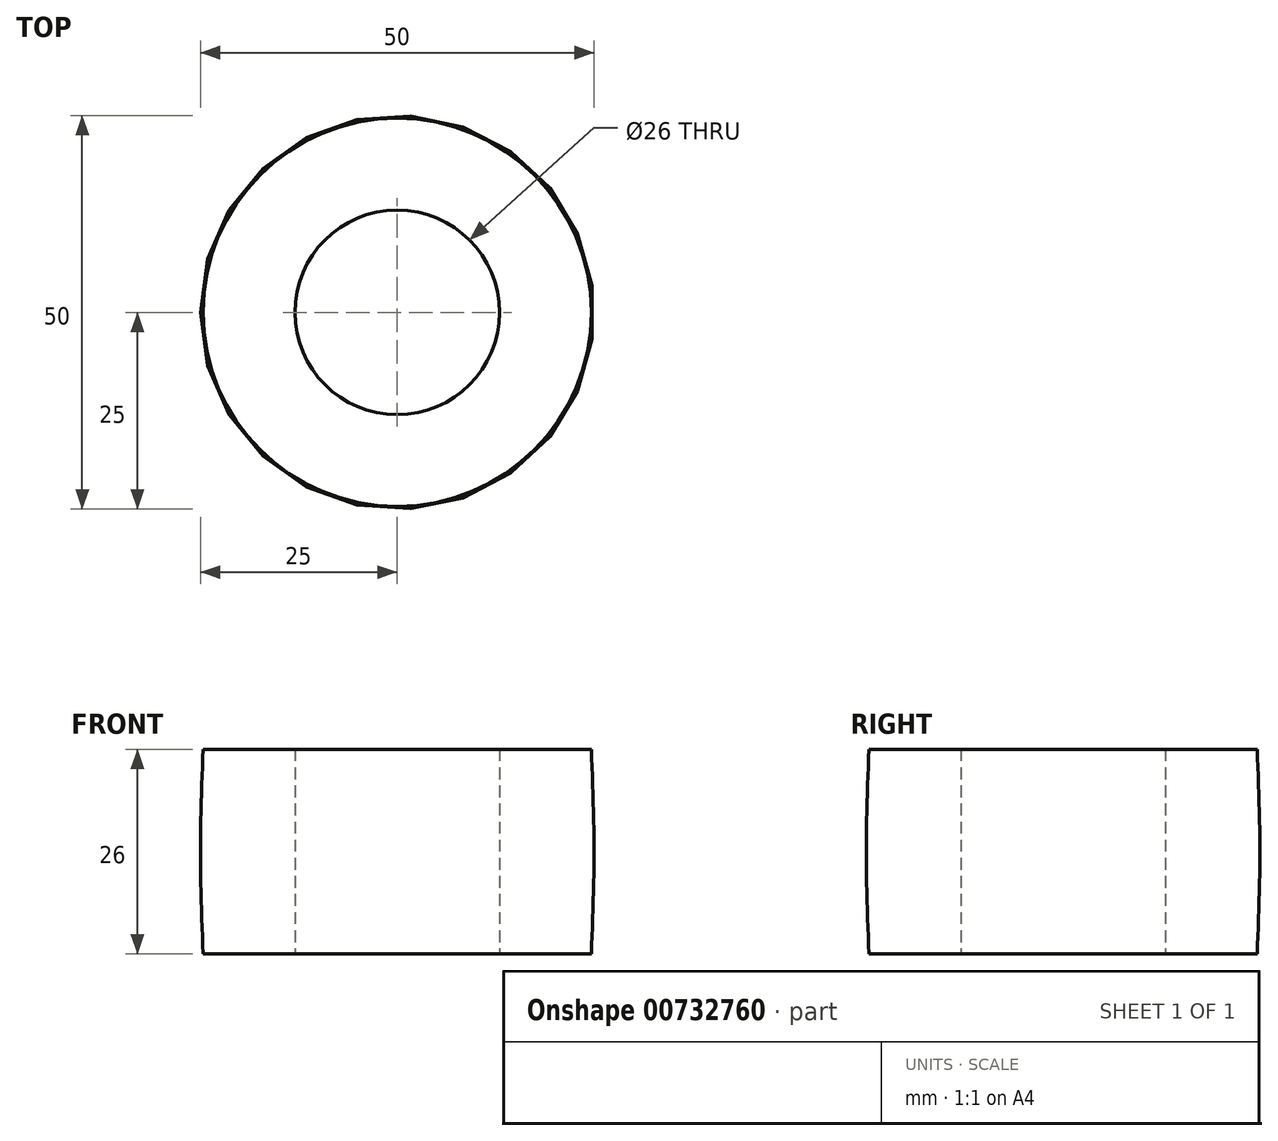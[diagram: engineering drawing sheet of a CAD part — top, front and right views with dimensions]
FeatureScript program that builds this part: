
annotation { "Feature Type Name" : "Feature", "Feature Type Description" : "" }
export const myFeature = defineFeature(function(context is Context, id is Id, definition is map)
    precondition{}
    {
        {
            var Q0;
            Q0=qCreatedBy(makeId("Top.planeOp"),FACE);
            var sketch = newSketch(context, id + "F0", { "sketchPlane" : qUnion([Q0])});
            skCircle(sketch, "E0", {"center": v(0, 0) * mm, "radius": 13 * mm});
            skCircle(sketch, "E1", {"center": v(0, 0) * mm, "radius": 25 * mm});
            skSolve(sketch);
        }
        {
            var Q0;
            Q0=makeQuery(id+"F0.imprint","IMPRINT",FACE,{"disambiguationData":[TD([[makeQuery(id+"F0.imprint","IMPRINT",EDGE,{"derivedFrom":sQuery(id+"F0.wireOp",EDGE,"E0")}),-1.0]])]});
            extrude(context, id + "F1", {"entities" : qUnion([Q0]), "endBound" : BoundingType.SYMMETRIC, "depth" : 26 * mm, "offsetDistance" : 25 * mm});
        }
        {
            var Q0;
            Q0=qCreatedBy(makeId("Front.planeOp"),FACE);
            var sketch = newSketch(context, id + "F2", { "sketchPlane" : qUnion([Q0])});
            skLineSegment(sketch, "E2.bottom", {"start": v(-24.66, 13) * mm, "end": v(-43.25, 13) * mm});
            skLineSegment(sketch, "E2.top", {"start": v(-24.66, -13) * mm, "end": v(-43.25, -13) * mm});
            skLineSegment(sketch, "E2.left", {"start": v(-24.66, 13) * mm, "end": v(-24.66, -13) * mm});
            skLineSegment(sketch, "E2.right", {"start": v(-43.25, 13) * mm, "end": v(-43.25, -13) * mm});
            skLineSegment(sketch, "E3", {"start": v(-24.66, 13) * mm, "end": v(-25, 0) * mm, "construction": true});
            skLineSegment(sketch, "E4", {"start": v(-24.66, -13) * mm, "end": v(-25, 0) * mm, "construction": true});
            skFitSpline(sketch, "E5", {"points": [v(-24.66, -13) * mm, v(-25, 0) * mm, v(-24.66, 13) * mm], "startDerivative": vector(-1.02, 26) * mm, "endDerivative": vector(1.02, 26) * mm});
            skLineSegment(sketch, "E6", {"start": v(0, 13.98) * mm, "end": v(0, -14.3) * mm});
            skSolve(sketch);
        }
        {
            var Q0;
            Q0=makeQuery(id+"F2.imprint","IMPRINT",FACE,{"disambiguationData":[TD([[makeQuery(id+"F2.imprint","IMPRINT",EDGE,{"derivedFrom":sQuery(id+"F2.wireOp",EDGE,"E2.bottom")}),1.0]])]});
            var Q1;
            Q1=sQuery(id+"F2.wireOp",EDGE,"E6");
            revolve(context, id + "F3", {"operationType" : NewBodyOperationType.REMOVE, "surfaceOperationType" : NewSurfaceOperationType.NEW, "entities" : qUnion([Q0]), "axis" : qUnion([Q1]), "revolveType" : RevolveType.FULL, "oppositeDirection" : true});
        }
    });
